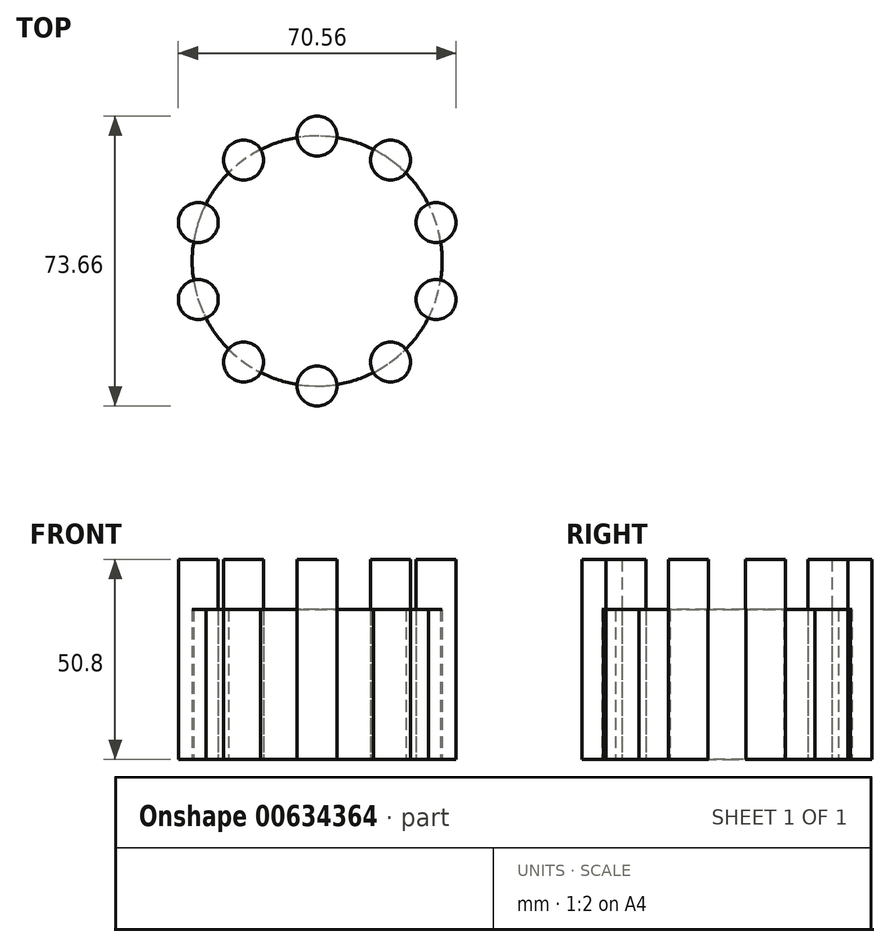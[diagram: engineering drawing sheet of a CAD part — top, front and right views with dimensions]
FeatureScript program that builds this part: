
annotation { "Feature Type Name" : "Feature", "Feature Type Description" : "" }
export const myFeature = defineFeature(function(context is Context, id is Id, definition is map)
    precondition{}
    {
        {
            var Q0;
            Q0=qCreatedBy(makeId("Top.planeOp"),FACE);
            var sketch = newSketch(context, id + "F0", { "sketchPlane" : qUnion([Q0])});
            skCircle(sketch, "E0", {"center": v(0, 0) * mm, "radius": 31.75 * mm});
            skSolve(sketch);
        }
        {
            var Q0;
            Q0=qSketchRegion(id+"F0",true);
            extrude(context, id + "F1", {"entities" : qUnion([Q0]), "depth" : 38.1 * mm});
        }
        {
            var Q0;
            Q0=qCreatedBy(makeId("Top.planeOp"),FACE);
            var sketch = newSketch(context, id + "F2", { "sketchPlane" : qUnion([Q0])});
            skCircle(sketch, "E1", {"center": v(0, 31.75) * mm, "radius": 5.08 * mm});
            skCircle(sketch, "E2.1.0", {"center": v(-18.66, 25.69) * mm, "radius": 5.08 * mm});
            skCircle(sketch, "E2.2.0", {"center": v(-30.2, 9.81) * mm, "radius": 5.08 * mm});
            skCircle(sketch, "E2.3.0", {"center": v(-30.2, -9.81) * mm, "radius": 5.08 * mm});
            skCircle(sketch, "E2.4.0", {"center": v(-18.66, -25.69) * mm, "radius": 5.08 * mm});
            skCircle(sketch, "E2.5.0", {"center": v(0, -31.75) * mm, "radius": 5.08 * mm});
            skCircle(sketch, "E2.6.0", {"center": v(18.66, -25.69) * mm, "radius": 5.08 * mm});
            skCircle(sketch, "E2.7.0", {"center": v(30.2, -9.81) * mm, "radius": 5.08 * mm});
            skCircle(sketch, "E2.8.0", {"center": v(30.2, 9.81) * mm, "radius": 5.08 * mm});
            skCircle(sketch, "E2.9.0", {"center": v(18.66, 25.69) * mm, "radius": 5.08 * mm});
            skPoint(sketch, "E2.center", {"position": v(0, 0) * mm});
            skSolve(sketch);
        }
        {
            var Q0;
            Q0=qSketchRegion(id+"F2",true);
            extrude(context, id + "F3", {"entities" : qUnion([Q0]), "depth" : 50.8 * mm});
        }
        {
            var Q0;
            Q0=makeQuery(id+"F3.opExtrude","SWEPT_BODY",BODY,{"disambiguationData":[OSD([sQuery(id+"F2.wireOp",EDGE,"E2.1.0")])]});
            var Q1;
            Q1=makeQuery(id+"F1.opExtrude","SWEPT_BODY",BODY,{"disambiguationData":[OSD([sQuery(id+"F0.wireOp",EDGE,"E0")])]});
            booleanBodies(context, id + "F4", {"operationType" : BooleanOperationType.INTERSECTION, "tools" : qUnion([Q0, Q1]), "keepTools" : true});
        }
        {
            var Q0;
            Q0=makeQuery(id+"F3.opExtrude","SWEPT_BODY",BODY,{"disambiguationData":[OSD([sQuery(id+"F2.wireOp",EDGE,"E2.2.0")])]});
            var Q1;
            Q1=makeQuery(id+"F1.opExtrude","SWEPT_BODY",BODY,{"disambiguationData":[OSD([sQuery(id+"F0.wireOp",EDGE,"E0")])]});
            booleanBodies(context, id + "F5", {"operationType" : BooleanOperationType.INTERSECTION, "tools" : qUnion([Q0, Q1]), "keepTools" : true});
        }
        {
            var Q0;
            Q0=makeQuery(id+"F3.opExtrude","SWEPT_BODY",BODY,{"disambiguationData":[OSD([sQuery(id+"F2.wireOp",EDGE,"E2.3.0")])]});
            var Q1;
            Q1=makeQuery(id+"F1.opExtrude","SWEPT_BODY",BODY,{"disambiguationData":[OSD([sQuery(id+"F0.wireOp",EDGE,"E0")])]});
            booleanBodies(context, id + "F6", {"operationType" : BooleanOperationType.INTERSECTION, "tools" : qUnion([Q0, Q1]), "keepTools" : true});
        }
        {
            var Q0;
            Q0=makeQuery(id+"F3.opExtrude","SWEPT_BODY",BODY,{"disambiguationData":[OSD([sQuery(id+"F2.wireOp",EDGE,"E2.4.0")])]});
            var Q1;
            Q1=makeQuery(id+"F1.opExtrude","SWEPT_BODY",BODY,{"disambiguationData":[OSD([sQuery(id+"F0.wireOp",EDGE,"E0")])]});
            booleanBodies(context, id + "F7", {"operationType" : BooleanOperationType.INTERSECTION, "tools" : qUnion([Q0, Q1]), "keepTools" : true});
        }
        {
            var Q0;
            Q0=makeQuery(id+"F3.opExtrude","SWEPT_BODY",BODY,{"disambiguationData":[OSD([sQuery(id+"F2.wireOp",EDGE,"E2.5.0")])]});
            var Q1;
            Q1=makeQuery(id+"F1.opExtrude","SWEPT_BODY",BODY,{"disambiguationData":[OSD([sQuery(id+"F0.wireOp",EDGE,"E0")])]});
            booleanBodies(context, id + "F8", {"operationType" : BooleanOperationType.INTERSECTION, "tools" : qUnion([Q0, Q1]), "keepTools" : true});
        }
        {
            var Q0;
            Q0=makeQuery(id+"F3.opExtrude","SWEPT_BODY",BODY,{"disambiguationData":[OSD([sQuery(id+"F2.wireOp",EDGE,"E2.6.0")])]});
            var Q1;
            Q1=makeQuery(id+"F1.opExtrude","SWEPT_BODY",BODY,{"disambiguationData":[OSD([sQuery(id+"F0.wireOp",EDGE,"E0")])]});
            booleanBodies(context, id + "F9", {"operationType" : BooleanOperationType.INTERSECTION, "tools" : qUnion([Q0, Q1]), "keepTools" : true});
        }
        {
            var Q0;
            Q0=makeQuery(id+"F3.opExtrude","SWEPT_BODY",BODY,{"disambiguationData":[OSD([sQuery(id+"F2.wireOp",EDGE,"E2.7.0")])]});
            var Q1;
            Q1=makeQuery(id+"F1.opExtrude","SWEPT_BODY",BODY,{"disambiguationData":[OSD([sQuery(id+"F0.wireOp",EDGE,"E0")])]});
            booleanBodies(context, id + "F10", {"operationType" : BooleanOperationType.INTERSECTION, "tools" : qUnion([Q0, Q1]), "keepTools" : true});
        }
        {
            var Q0;
            Q0=makeQuery(id+"F3.opExtrude","SWEPT_BODY",BODY,{"disambiguationData":[OSD([sQuery(id+"F2.wireOp",EDGE,"E2.8.0")])]});
            var Q1;
            Q1=makeQuery(id+"F1.opExtrude","SWEPT_BODY",BODY,{"disambiguationData":[OSD([sQuery(id+"F0.wireOp",EDGE,"E0")])]});
            booleanBodies(context, id + "F11", {"operationType" : BooleanOperationType.INTERSECTION, "tools" : qUnion([Q0, Q1]), "keepTools" : true});
        }
        {
            var Q0;
            Q0=makeQuery(id+"F3.opExtrude","SWEPT_BODY",BODY,{"disambiguationData":[OSD([sQuery(id+"F2.wireOp",EDGE,"E2.9.0")])]});
            var Q1;
            Q1=makeQuery(id+"F1.opExtrude","SWEPT_BODY",BODY,{"disambiguationData":[OSD([sQuery(id+"F0.wireOp",EDGE,"E0")])]});
            booleanBodies(context, id + "F12", {"operationType" : BooleanOperationType.INTERSECTION, "tools" : qUnion([Q0, Q1]), "keepTools" : true});
        }
        {
            var Q0;
            Q0=makeQuery(id+"F3.opExtrude","SWEPT_BODY",BODY,{"disambiguationData":[OSD([sQuery(id+"F2.wireOp",EDGE,"E1")])]});
            var Q1;
            Q1=makeQuery(id+"F1.opExtrude","SWEPT_BODY",BODY,{"disambiguationData":[OSD([sQuery(id+"F0.wireOp",EDGE,"E0")])]});
            booleanBodies(context, id + "F13", {"operationType" : BooleanOperationType.INTERSECTION, "tools" : qUnion([Q0, Q1]), "keepTools" : true});
        }
        {
            var Q0;
            Q0=makeQuery(id+"F3.opExtrude","SWEPT_BODY",BODY,{"disambiguationData":[OSD([sQuery(id+"F2.wireOp",EDGE,"E1")])]});
            var Q1;
            Q1=makeQuery(id+"F1.opExtrude","SWEPT_BODY",BODY,{"disambiguationData":[OSD([sQuery(id+"F0.wireOp",EDGE,"E0")])]});
            booleanBodies(context, id + "F14", {"operationType" : BooleanOperationType.INTERSECTION, "tools" : qUnion([Q0, Q1]), "keepTools" : true});
        }
    });
